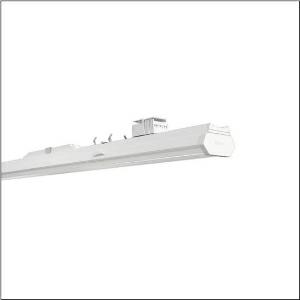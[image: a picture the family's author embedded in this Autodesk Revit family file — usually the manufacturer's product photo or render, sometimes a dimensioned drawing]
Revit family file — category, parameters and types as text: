
# Revit family: licross_r__21_protected_mo_52td12cn49xg_6de8
name_source: partatom
category: Lighting Fixtures
units: mm (PartAtom-declared; Revit-internal decimal feet)

## family parameters
Cut with Voids When Loaded = No
Host = Face
Light Source = No
Part Type = Normal
Room Calculation Point = No
Round Connector Dimension = Use Diameter
Shared = No

## types (1)
- --- (1 x LED, 9110 lm, 50.4 W, 4000K)
    Apparent Load = 50 VA
    CIE Flux Codes = 73 92 98 99 100
    Color Rendering = 80
    Color Temperature = 4000K
    Default Elevation = 1800 mm
    Description = Licross® 21 Protected MO, luminaire insert, of sheet steel, galvanised, coil coated, white, length: 1.500mm, width: 90mm, height: 103mm, LED rated luminous flux: 9.120lm, light colour: 840, control gear: ON/OFF Multilumen, CLOi, control gear: ECG Multilumen, with plug, 3-pole, with phase selection, mains connection: 220..240V, AC, 50/60Hz, start of lifetime: 50W, end of service life: 61W, internal wiring halogen-free, primary light control with lens, of plastic, primary optical cover: cover, of PMMA, light emission: direct distribution, primary light characteristic: symmetric, protection rating (complete): IP54, insulation class (complete): insulation class I (protective earthing), certification: CE, ENEC, VDE, UKCA, protection symbol: D if used in an environment with non-conductive dust loads with corresponding accessories, impact resistance: IK06, permissible ambient temperature for indoor applications: -35..+45°C, corresponds to IFS (International Featured Standards) requirements for safety and quality in the food industry, reducing of maximum allowable ambient temperature of 5°C with ceiling mounting, LABS conformity tested according to VDMA 24364:2018-05, packaging unit: 1 piece
    Height = 92 mm
    Lamp = 1 x LED
    Lamp Light Flux = 9110 lm
    Lamp Power = 50.4 W
    Lamp count = 1
    Length = 1500 mm
    Luminous efficacy = 181 lm/W
    Manufacturer = Siteco
    ModVariant = No
    Model = 52TD12CN49XG
    Mounting Place = Ceiling
    Mounting Type = Pendant
    Number of Poles = 1
    OnlyDefault = Yes
    Power Factor = 1
    Product Name = Licross® 21 Protected MO
    Product group = luminaire insert | ceiling pendant
    ProductGroupID = 902
    Protection Class = Protection class I
    Protection Degree = IP 54
    RLX_Detail_Level = 1
    RLX_Emergency_Light_Flux = 0 lm
    RLX_Emergency_Type = 0
    RLX_Emergency_Type_DB = No
    RlxData = <blob elided: 22313 chars, md5=c5f86433>
    Socket = socket
    Standby Power = 0 W
    System Light Flux = 9110 lm
    System Power = 50 W
    Type Comments = factory setting: luminous flux: 100 % | (A | C | E) | 117 mA
    Type Image = l_1256148.jpg
    URL = http://relux.com
    VarID = @adj_132683
    Voltage = 0 V
    Weight = 0.00 kg
    Width = 88 mm

## geometry (parser evidence)
native form markers: Blend x4, Sweep x11
no freeform markers — native parametric forms only
